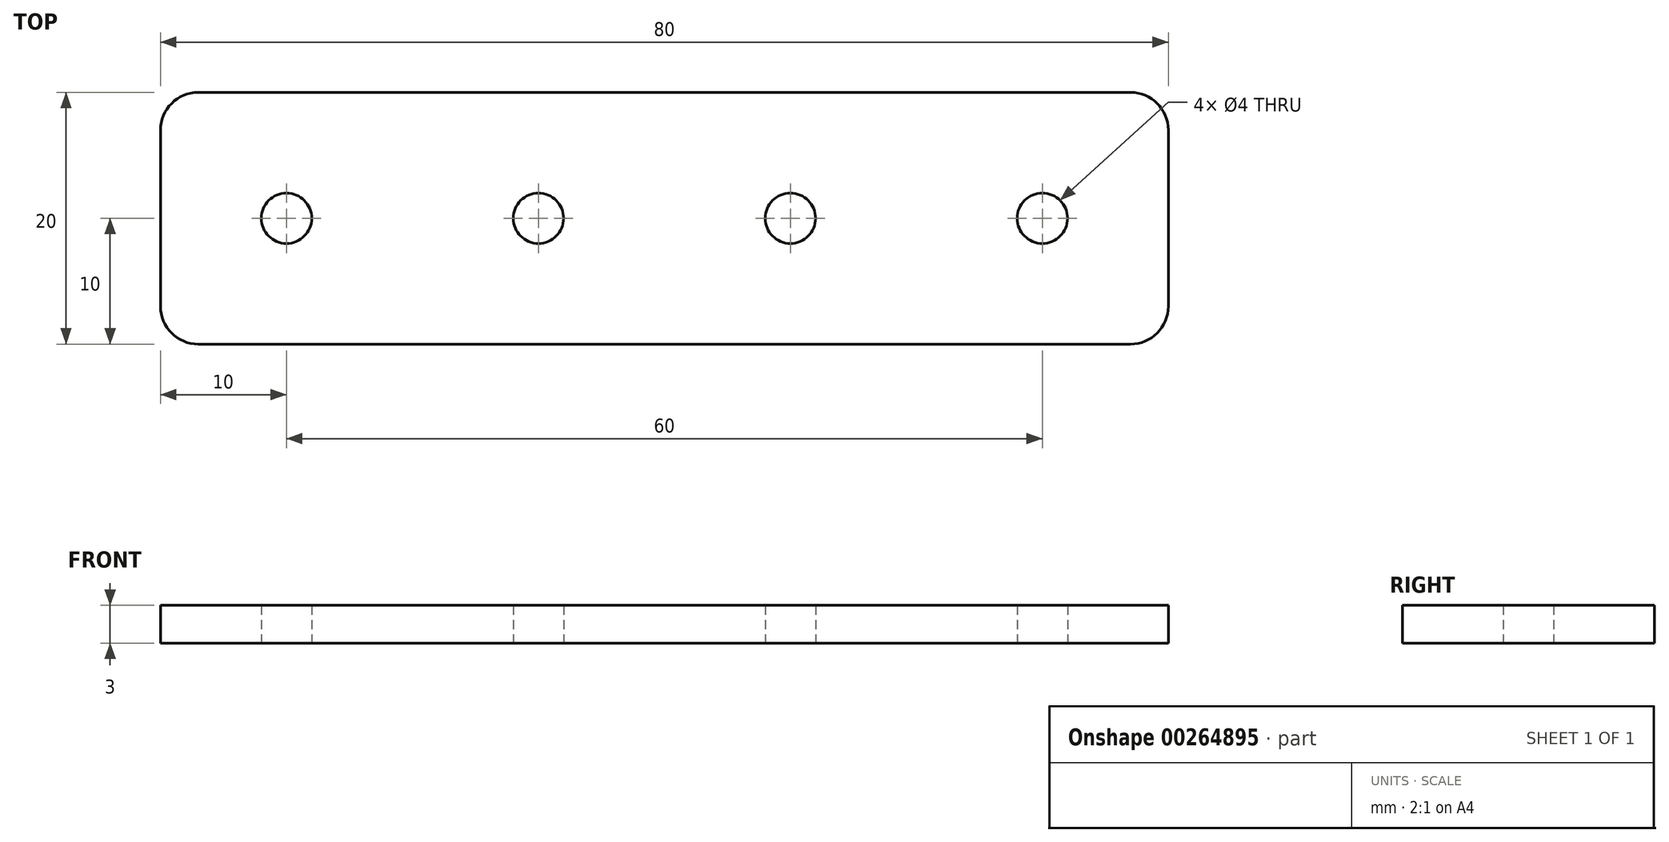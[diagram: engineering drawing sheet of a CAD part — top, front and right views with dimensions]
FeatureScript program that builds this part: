
annotation { "Feature Type Name" : "Feature", "Feature Type Description" : "" }
export const myFeature = defineFeature(function(context is Context, id is Id, definition is map)
    precondition{}
    {
        {
            var Q0;
            Q0=qCreatedBy(makeId("Top.planeOp"),FACE);
            var sketch = newSketch(context, id + "F0", { "sketchPlane" : qUnion([Q0])});
            skLineSegment(sketch, "E0.bottom", {"start": v(37, -10) * mm, "end": v(-37, -10) * mm});
            skLineSegment(sketch, "E0.top", {"start": v(37, 10) * mm, "end": v(-37, 10) * mm});
            skLineSegment(sketch, "E0.left", {"start": v(40, -7) * mm, "end": v(40, 7) * mm});
            skLineSegment(sketch, "E0.right", {"start": v(-40, -7) * mm, "end": v(-40, 7) * mm});
            skPoint(sketch, "E0.middle", {"position": v(0, 0) * mm});
            skCircle(sketch, "E1", {"center": v(-30, 0) * mm, "radius": 2 * mm});
            skPoint(sketch, "E2.visualSharp", {"position": v(40, 10) * mm});
            skArc(sketch, "E2.filletArc", {"start": v(40, 7) * mm, "mid": v(39.12, 9.12) * mm, "end": v(37, 10) * mm});
            skPoint(sketch, "E3.visualSharp", {"position": v(40, -10) * mm});
            skArc(sketch, "E3.filletArc", {"start": v(37, -10) * mm, "mid": v(39.12, -9.12) * mm, "end": v(40, -7) * mm});
            skPoint(sketch, "E4.visualSharp", {"position": v(-40, -10) * mm});
            skArc(sketch, "E4.filletArc", {"start": v(-40, -7) * mm, "mid": v(-39.12, -9.12) * mm, "end": v(-37, -10) * mm});
            skPoint(sketch, "E5.visualSharp", {"position": v(-40, 10) * mm});
            skArc(sketch, "E5.filletArc", {"start": v(-37, 10) * mm, "mid": v(-39.12, 9.12) * mm, "end": v(-40, 7) * mm});
            skCircle(sketch, "E6.1.0.0", {"center": v(-10, 0) * mm, "radius": 2 * mm});
            skCircle(sketch, "E6.2.0.0", {"center": v(10, 0) * mm, "radius": 2 * mm});
            skCircle(sketch, "E6.3.0.0", {"center": v(30, 0) * mm, "radius": 2 * mm});
            skLineSegment(sketch, "E6.direction1", {"start": v(-30, 0) * mm, "end": v(-10, 0) * mm, "construction": true});
            skSolve(sketch);
        }
        {
            var Q0;
            Q0 = qSketchRegion(id + "F0", true);
            extrude(context, id + "F1", {"entities" : qUnion([Q0]), "depth" : 3 * mm});
        }
    });
